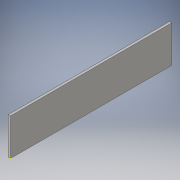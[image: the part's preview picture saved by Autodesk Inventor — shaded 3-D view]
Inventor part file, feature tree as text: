
AUTODESK INVENTOR PART (.ipt)
format: ipt  version: 2016 (Build 200138000, 138)  size: 91,136 bytes
history: native  units: in
note: dims shown in document units (in); Inventor stores cm internally (conversion verified against a paired STEP export)
features: sketch x2, extrude x1
ambient origin geometry x8: Origin, YZ Plane, XZ Plane, XY Plane, X Axis, Y Axis, Z Axis, Center Point
bodies: Solid1 (feature_tree)
feature tree (3):
  extrude  "Extrusion1"  Depth=17.5in
  sketch  "Sketch3"  dims[d4=2.0in d5=1.5in d6=2.0in d7=1.5in d8=0.25in d9=0.0in]
  sketch  "Sketch1"  dims[d2=4.0in d3=17.5in]
